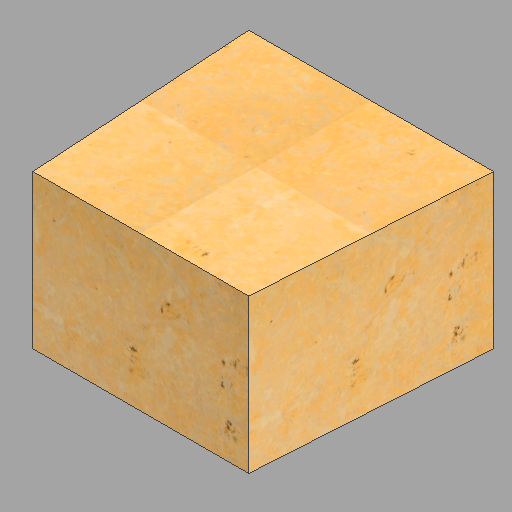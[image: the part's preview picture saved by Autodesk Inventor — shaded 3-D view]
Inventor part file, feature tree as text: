
AUTODESK INVENTOR PART (.ipt)
format: ipt  version: 2023 (Build 270158030, 158C)  size: 398,848 bytes
history: native  units: in
note: dims shown in document units (in); Inventor stores cm internally (conversion verified against a paired STEP export)
features: extrude x1, sketch x1
ambient origin geometry x8: Origin, YZ Plane, XZ Plane, XY Plane, X Axis, Y Axis, Z Axis, Center Point
bodies: Body1 (feature_tree)
feature tree (2):
  extrude  "Extrusion1"  Depth=36.0in
  sketch  "Sketch1"  dims[d0=38.25in d2=36.0in d3=0.0493in d4=2.2555in d5=2.2555in d6=24.0in d7=0.0in]
